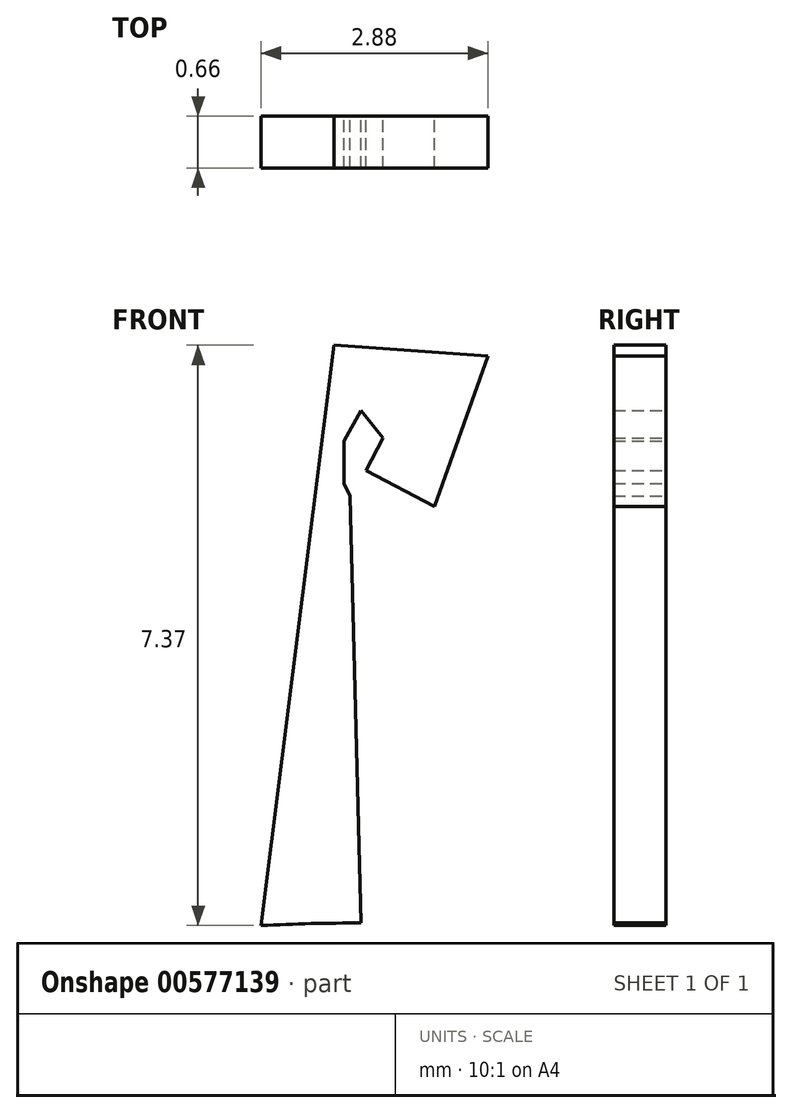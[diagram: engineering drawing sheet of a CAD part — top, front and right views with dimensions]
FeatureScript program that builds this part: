
annotation { "Feature Type Name" : "Feature", "Feature Type Description" : "" }
export const myFeature = defineFeature(function(context is Context, id is Id, definition is map)
    precondition{}
    {
        {
            var Q0;
            Q0=qCreatedBy(makeId("Front.planeOp"),FACE);
            var sketch = newSketch(context, id + "F0", { "sketchPlane" : qUnion([Q0])});
            skCircle(sketch, "E0", {"center": v(0, 0) * mm, "radius": 25.4 * mm});
            skLineSegment(sketch, "E1", {"start": v(0, 25.4) * mm, "end": v(-1.27, 25.37) * mm});
            skLineSegment(sketch, "E2", {"start": v(-1.27, 25.37) * mm, "end": v(0, 25.4) * mm});
            skLineSegment(sketch, "E3", {"start": v(0, 25.4) * mm, "end": v(1.27, 25.37) * mm});
            skLineSegment(sketch, "E4", {"start": v(-1.27, 25.37) * mm, "end": v(-0.35, 32.74) * mm});
            skLineSegment(sketch, "E5", {"start": v(-0.35, 32.74) * mm, "end": v(1.61, 32.6) * mm});
            skLineSegment(sketch, "E6", {"start": v(1.61, 32.6) * mm, "end": v(0.93, 30.7) * mm});
            skLineSegment(sketch, "E7", {"start": v(0.93, 30.7) * mm, "end": v(0.06, 31.15) * mm});
            skLineSegment(sketch, "E8", {"start": v(0.06, 31.15) * mm, "end": v(0.28, 31.56) * mm});
            skLineSegment(sketch, "E9", {"start": v(0.28, 31.56) * mm, "end": v(0, 31.91) * mm});
            skLineSegment(sketch, "E10", {"start": v(0, 31.91) * mm, "end": v(-0.22, 31.52) * mm});
            skLineSegment(sketch, "E11", {"start": v(-0.22, 31.52) * mm, "end": v(-0.22, 30.99) * mm});
            skLineSegment(sketch, "E12", {"start": v(-0.22, 30.99) * mm, "end": v(-0.14, 30.83) * mm});
            skLineSegment(sketch, "E13", {"start": v(-0.14, 30.83) * mm, "end": v(0, 25.4) * mm});
            skSolve(sketch);
        }
        {
            var Q0;
            {var subQ0=sQuery(id+"F0.wireOp",EDGE,"E4");Q0=makeQuery(id+"F0.imprint","IMPRINT",FACE,{"disambiguationData":[TD([[makeQuery(id+"F0.imprint","IMPRINT",EDGE,{"derivedFrom":subQ0}),-1.0]])]});}
            var Q1;
            {var subQ0=sQuery(id+"F0.wireOp",EDGE,"E2");Q1=makeQuery(id+"F0.imprint","IMPRINT",FACE,{"disambiguationData":[TD([[makeQuery(id+"F0.imprint","IMPRINT",EDGE,{"derivedFrom":subQ0}),-1.0]])]});}
            extrude(context, id + "F1", {"entities" : qUnion([Q0, Q1]), "depth" : 0.66 * mm, "offsetDistance" : 25.4 * mm});
        }
    });
